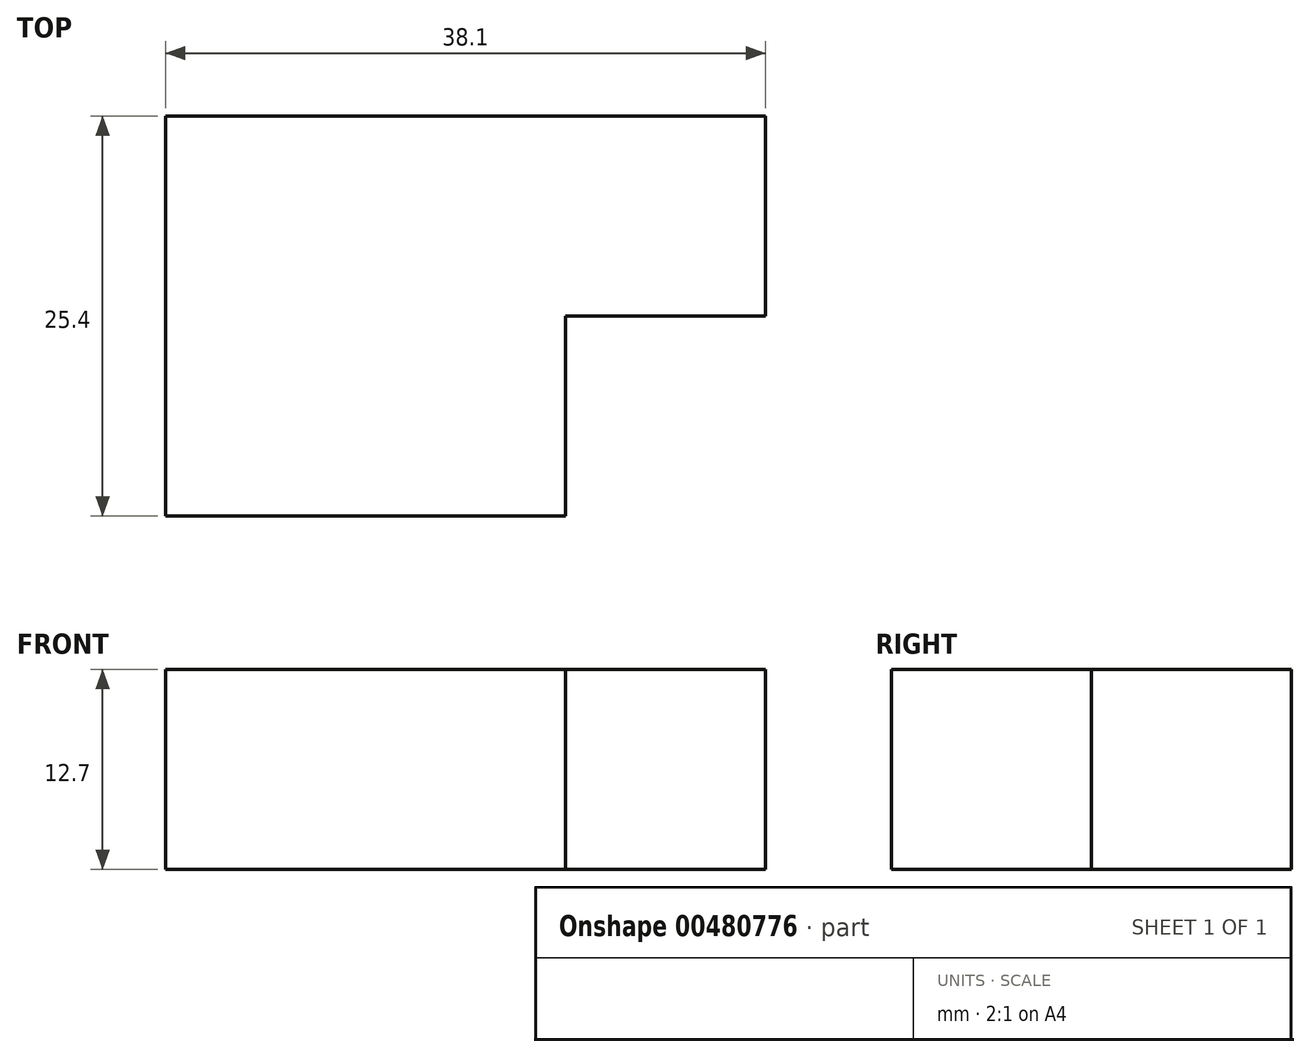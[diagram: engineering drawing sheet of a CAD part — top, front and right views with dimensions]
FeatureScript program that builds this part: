
annotation { "Feature Type Name" : "Feature", "Feature Type Description" : "" }
export const myFeature = defineFeature(function(context is Context, id is Id, definition is map)
    precondition{}
    {
        {
            var Q0;
            Q0=qCreatedBy(makeId("Top.planeOp"),FACE);
            var sketch = newSketch(context, id + "F0", { "sketchPlane" : qUnion([Q0])});
            skLineSegment(sketch, "E0", {"start": v(0, 0) * mm, "end": v(38.1, 0) * mm});
            skLineSegment(sketch, "E1", {"start": v(38.1, 0) * mm, "end": v(38.1, -12.7) * mm});
            skLineSegment(sketch, "E2", {"start": v(38.1, -12.7) * mm, "end": v(25.4, -12.7) * mm});
            skLineSegment(sketch, "E3", {"start": v(25.4, -12.7) * mm, "end": v(25.4, -25.4) * mm});
            skLineSegment(sketch, "E4", {"start": v(25.4, -25.4) * mm, "end": v(0, -25.4) * mm});
            skLineSegment(sketch, "E5", {"start": v(0, -25.4) * mm, "end": v(0, 0) * mm});
            skSolve(sketch);
        }
        {
            var Q0;
            Q0 = qSketchRegion(id + "F0", true);
            extrude(context, id + "F1", {"entities" : qUnion([Q0]), "depth" : 12.7 * mm});
        }
    });
